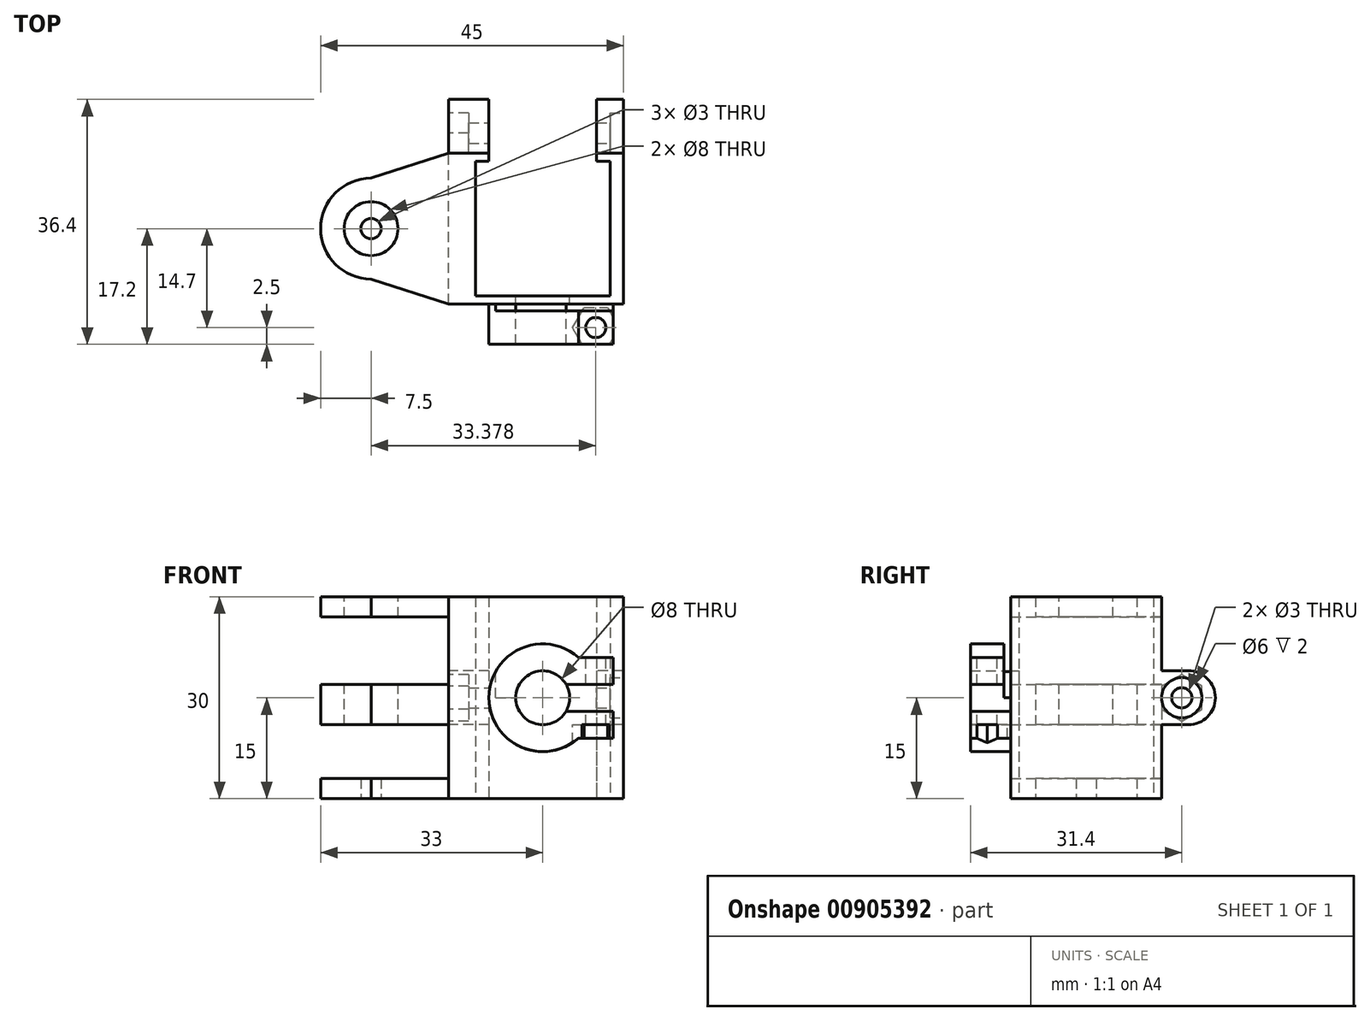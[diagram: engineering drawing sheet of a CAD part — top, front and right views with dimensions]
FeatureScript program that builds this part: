
annotation { "Feature Type Name" : "Feature", "Feature Type Description" : "" }
export const myFeature = defineFeature(function(context is Context, id is Id, definition is map)
    precondition{}
    {
        {
            var Q0;
            Q0=qCreatedBy(makeId("Top.planeOp"),FACE);
            var sketch = newSketch(context, id + "F0", { "sketchPlane" : qUnion([Q0])});
            skLineSegment(sketch, "E0.bottom", {"start": v(0, 0) * mm, "end": v(20, 0) * mm});
            skLineSegment(sketch, "E0.top", {"start": v(0, 20) * mm, "end": v(20, 20) * mm});
            skLineSegment(sketch, "E0.left", {"start": v(0, 0) * mm, "end": v(0, 20) * mm});
            skLineSegment(sketch, "E0.right", {"start": v(20, 0) * mm, "end": v(20, 20) * mm});
            skLineSegment(sketch, "E1.bottom", {"start": v(0, 0) * mm, "end": v(-4, 0) * mm, "construction": true});
            skLineSegment(sketch, "E1.top", {"start": v(0, -1.2) * mm, "end": v(-4, -1.2) * mm, "construction": true});
            skLineSegment(sketch, "E1.left", {"start": v(0, 0) * mm, "end": v(0, -1.2) * mm, "construction": true});
            skLineSegment(sketch, "E1.right", {"start": v(-4, 0) * mm, "end": v(-4, -1.2) * mm, "construction": true});
            skLineSegment(sketch, "E2.bottom", {"start": v(-4, -1.2) * mm, "end": v(22, -1.2) * mm});
            skLineSegment(sketch, "E2.top", {"start": v(-4, 21.2) * mm, "end": v(22, 21.2) * mm});
            skLineSegment(sketch, "E2.left", {"start": v(-4, -1.2) * mm, "end": v(-4, 21.2) * mm});
            skLineSegment(sketch, "E2.right", {"start": v(22, -1.2) * mm, "end": v(22, 21.2) * mm});
            skLineSegment(sketch, "E3", {"start": v(0, 20) * mm, "end": v(2, 20) * mm, "construction": true});
            skLineSegment(sketch, "E4", {"start": v(2, 20) * mm, "end": v(2, 21.2) * mm});
            skLineSegment(sketch, "E5", {"start": v(20, 20) * mm, "end": v(18, 20) * mm, "construction": true});
            skLineSegment(sketch, "E6", {"start": v(18, 20) * mm, "end": v(18, 21.2) * mm});
            skLineSegment(sketch, "E7.bottom", {"start": v(9, -1.2) * mm, "end": v(-6, -1.2) * mm, "construction": true});
            skLineSegment(sketch, "E7.top", {"start": v(9, 10) * mm, "end": v(-6, 10) * mm, "construction": true});
            skLineSegment(sketch, "E7.left", {"start": v(9, -1.2) * mm, "end": v(9, 10) * mm, "construction": true});
            skLineSegment(sketch, "E7.right", {"start": v(-6, -1.2) * mm, "end": v(-6, 10) * mm, "construction": true});
            skLineSegment(sketch, "E8", {"start": v(-6, 10) * mm, "end": v(-15.5, 10) * mm, "construction": true});
            skCircle(sketch, "E9", {"center": v(-15.5, 10) * mm, "radius": 7.5 * mm});
            skCircle(sketch, "E10", {"center": v(-15.5, 10) * mm, "radius": 1.5 * mm});
            skLineSegment(sketch, "E11", {"start": v(-15.5, 10) * mm, "end": v(-15.5, 17.5) * mm, "construction": true});
            skLineSegment(sketch, "E12", {"start": v(-15.5, 17.5) * mm, "end": v(-15.5, 2.5) * mm, "construction": true});
            skLineSegment(sketch, "E13", {"start": v(-4, -1.2) * mm, "end": v(-15.5, 2.5) * mm});
            skLineSegment(sketch, "E14", {"start": v(-4, 21.2) * mm, "end": v(-15.5, 17.5) * mm});
            skSolve(sketch);
        }
        {
            var Q0;
            Q0=makeQuery(id+"F0.imprint","IMPRINT",FACE,{"disambiguationData":[TD([[makeQuery(id+"F0.imprint","IMPRINT",EDGE,{"derivedFrom":sQuery(id+"F0.wireOp",EDGE,"E0.bottom")}),-1.0]])]});
            extrude(context, id + "F1", {"entities" : qUnion([Q0]), "depth" : 30 * mm, "offsetDistance" : 25 * mm});
        }
        {
            var Q0;
            Q0=makeQuery(id+"F1.opExtrude","SWEPT_FACE",FACE,{"disambiguationData":[OSD([sQuery(id+"F0.wireOp",EDGE,"E2.bottom")])]});
            var sketch = newSketch(context, id + "F2", { "sketchPlane" : qUnion([Q0])});
            skCircle(sketch, "E15", {"center": v(10, 15) * mm, "radius": 4 * mm});
            skCircle(sketch, "E16", {"center": v(10, 15) * mm, "radius": 8 * mm});
            skLineSegment(sketch, "E17", {"start": v(10, 15) * mm, "end": v(10, 13) * mm, "construction": true});
            skLineSegment(sketch, "E18", {"start": v(10, 13) * mm, "end": v(13.46, 13) * mm, "construction": true});
            skLineSegment(sketch, "E19", {"start": v(10, 15) * mm, "end": v(10, 17) * mm, "construction": true});
            skLineSegment(sketch, "E20", {"start": v(10, 17) * mm, "end": v(13.46, 17) * mm, "construction": true});
            skLineSegment(sketch, "E21", {"start": v(13.46, 17) * mm, "end": v(20.46, 17) * mm});
            skLineSegment(sketch, "E22", {"start": v(13.46, 17) * mm, "end": v(13.46, 21) * mm, "construction": true});
            skLineSegment(sketch, "E23", {"start": v(13.46, 21) * mm, "end": v(20.46, 21) * mm});
            skLineSegment(sketch, "E24", {"start": v(13.46, 13) * mm, "end": v(20.46, 13) * mm});
            skLineSegment(sketch, "E25", {"start": v(13.46, 13) * mm, "end": v(13.46, 9) * mm, "construction": true});
            skLineSegment(sketch, "E26", {"start": v(13.46, 9) * mm, "end": v(20.46, 9) * mm});
            skLineSegment(sketch, "E27", {"start": v(20.46, 9) * mm, "end": v(20.46, 13) * mm});
            skLineSegment(sketch, "E28", {"start": v(20.46, 21) * mm, "end": v(20.46, 17) * mm});
            skLineSegment(sketch, "E29", {"start": v(10, 15) * mm, "end": v(-4, 15) * mm});
            skSolve(sketch);
        }
        {
            var Q0;
            {var subQ5=sQuery(id+"F2.wireOp",EDGE,"E21");var subQ7=sQuery(id+"F2.wireOp",EDGE,"E15");var subQ8=makeQuery(id+"F2.imprint","INTERSECT",VERTEX,{"derivedFrom":[subQ7,subQ5]});Q0=makeQuery(id+"F2.imprint","IMPRINT",FACE,{"disambiguationData":[TD([[makeQuery(id+"F2.imprint","IMPRINT",EDGE,{"disambiguationData":[TD([[subQ8,-1.0]])],"derivedFrom":subQ7}),-1.0]])]});}
            var Q1;
            {var subQ5=sQuery(id+"F2.wireOp",EDGE,"E28");Q1=makeQuery(id+"F2.imprint","IMPRINT",FACE,{"disambiguationData":[TD([[makeQuery(id+"F2.imprint","IMPRINT",EDGE,{"derivedFrom":subQ5}),-1.0]])]});}
            var Q2;
            {var subQ5=sQuery(id+"F2.wireOp",EDGE,"E27");Q2=makeQuery(id+"F2.imprint","IMPRINT",FACE,{"disambiguationData":[TD([[makeQuery(id+"F2.imprint","IMPRINT",EDGE,{"derivedFrom":subQ5}),1.0]])]});}
            var Q3;
            {var subQ4=sQuery(id+"F2.wireOp",EDGE,"E15");var subQ6=sQuery(id+"F2.wireOp",EDGE,"E24");var subQ7=makeQuery(id+"F2.imprint","INTERSECT",VERTEX,{"derivedFrom":[subQ4,subQ6]});Q3=makeQuery(id+"F2.imprint","IMPRINT",FACE,{"disambiguationData":[TD([[makeQuery(id+"F2.imprint","IMPRINT",EDGE,{"disambiguationData":[TD([[subQ7,1.0]])],"derivedFrom":subQ4}),-1.0]])]});}
            extrude(context, id + "F3", {"entities" : qUnion([Q0, Q1, Q2, Q3]), "operationType" : NewBodyOperationType.ADD, "depth" : 6 * mm, "offsetDistance" : 25 * mm});
        }
        {
            var Q0;
            {var subQ0=sQuery(id+"F2.wireOp",EDGE,"E15");var subQ1=makeQuery(id+"F2.imprint","INTERSECT",VERTEX,{"derivedFrom":[subQ0,sQuery(id+"F2.wireOp",EDGE,"E21")]});Q0=makeQuery(id+"F2.imprint","IMPRINT",FACE,{"disambiguationData":[TD([[makeQuery(id+"F2.imprint","IMPRINT",EDGE,{"disambiguationData":[TD([[subQ1,-1.0]])],"derivedFrom":subQ0}),1.0]])]});}
            extrude(context, id + "F4", {"entities" : qUnion([Q0]), "operationType" : NewBodyOperationType.REMOVE, "oppositeDirection" : true, "depth" : 25 * mm, "offsetDistance" : 25 * mm});
        }
        {
            var Q0;
            Q0=makeQuery(id+"F1.opExtrude","CAP_FACE",FACE,{"disambiguationData":[OSD([sQuery(id+"F0.wireOp",EDGE,"E0.bottom"),sQuery(id+"F0.wireOp",EDGE,"E0.left"),sQuery(id+"F0.wireOp",EDGE,"E0.right"),sQuery(id+"F0.wireOp",EDGE,"E2.bottom"),sQuery(id+"F0.wireOp",EDGE,"E2.top"),sQuery(id+"F0.wireOp",EDGE,"E2.left"),sQuery(id+"F0.wireOp",EDGE,"E2.right"),sQuery(id+"F0.wireOp",EDGE,"0gwIZlqe-FvKl-Nv9Y-vsOx-YCTr08s2W5oZ"),sQuery(id+"F0.wireOp",EDGE,"uGnjY2x7-gKUO-HtRP-5AOL-VpCL24SmFymk")])],"isStart":false});
            var sketch = newSketch(context, id + "F5", { "sketchPlane" : qUnion([Q0])});
            skLineSegment(sketch, "E30", {"start": v(0, 0) * mm, "end": v(3, 0) * mm, "construction": true});
            skLineSegment(sketch, "E31", {"start": v(3, 0) * mm, "end": v(3, -1.2) * mm, "construction": true});
            skLineSegment(sketch, "E32.bottom", {"start": v(3, -1.2) * mm, "end": v(23, -1.2) * mm});
            skLineSegment(sketch, "E32.top", {"start": v(3, -2.2) * mm, "end": v(23, -2.2) * mm});
            skLineSegment(sketch, "E32.left", {"start": v(3, -1.2) * mm, "end": v(3, -2.2) * mm});
            skLineSegment(sketch, "E32.right", {"start": v(23, -1.2) * mm, "end": v(23, -2.2) * mm});
            skSolve(sketch);
        }
        {
            var Q0;
            Q0=makeQuery(id+"F5.imprint","IMPRINT",FACE,{"disambiguationData":[TD([[makeQuery(id+"F5.imprint","IMPRINT",EDGE,{"derivedFrom":sQuery(id+"F5.wireOp",EDGE,"E32.top")}),1.0]])]});
            extrude(context, id + "F6", {"entities" : qUnion([Q0]), "operationType" : NewBodyOperationType.REMOVE, "oppositeDirection" : true, "depth" : 15 * mm, "offsetDistance" : 25 * mm});
        }
        {
            var Q0;
            Q0=makeQuery(id+"F3.opExtrude","SWEPT_FACE",FACE,{"disambiguationData":[OSD([sQuery(id+"F2.wireOp",EDGE,"E23")])]});
            var sketch = newSketch(context, id + "F7", { "sketchPlane" : qUnion([Q0])});
            skLineSegment(sketch, "E33", {"start": v(17.88, -7.2) * mm, "end": v(17.88, -4.7) * mm, "construction": true});
            skCircle(sketch, "E34", {"center": v(17.88, -4.7) * mm, "radius": 1.5 * mm});
            skSolve(sketch);
        }
        {
            var Q0;
            Q0=makeQuery(id+"F7.imprint","IMPRINT",FACE,{"disambiguationData":[TD([[makeQuery(id+"F7.imprint","IMPRINT",EDGE,{"derivedFrom":sQuery(id+"F7.wireOp",EDGE,"E34")}),1.0]])]});
            extrude(context, id + "F8", {"entities" : qUnion([Q0]), "operationType" : NewBodyOperationType.REMOVE, "oppositeDirection" : true, "depth" : 25 * mm, "offsetDistance" : 25 * mm});
        }
        {
            var Q0;
            {var subQ0=sQuery(id+"F0.wireOp",EDGE,"E2.top");Q0=makeQuery(id+"F1.opExtrude","SWEPT_FACE",FACE,{"disambiguationData":[OSD([subQ0]),TDD([makeQuery(id+"F0.imprint","IMPRINT",EDGE,{"disambiguationData":[TD([[makeQuery(id+"F0.imprint","INTERSECT",VERTEX,{"derivedFrom":[subQ0,sQuery(id+"F0.wireOp",EDGE,"E2.right")]}),1.0]])],"derivedFrom":subQ0})])]});}
            var sketch = newSketch(context, id + "F9", { "sketchPlane" : qUnion([Q0])});
            skLineSegment(sketch, "E35", {"start": v(-22, 30) * mm, "end": v(-22, 19) * mm, "construction": true});
            skLineSegment(sketch, "E36.bottom", {"start": v(-22, 19) * mm, "end": v(-18, 19) * mm});
            skLineSegment(sketch, "E36.top", {"start": v(-22, 11) * mm, "end": v(-18, 11) * mm});
            skLineSegment(sketch, "E36.left", {"start": v(-22, 19) * mm, "end": v(-22, 11) * mm});
            skLineSegment(sketch, "E36.right", {"start": v(-18, 19) * mm, "end": v(-18, 11) * mm});
            skLineSegment(sketch, "E37", {"start": v(-18, 11) * mm, "end": v(-2, 11) * mm, "construction": true});
            skLineSegment(sketch, "E38.bottom", {"start": v(-2, 11) * mm, "end": v(4, 11) * mm});
            skLineSegment(sketch, "E38.top", {"start": v(-2, 19) * mm, "end": v(4, 19) * mm});
            skLineSegment(sketch, "E38.left", {"start": v(-2, 11) * mm, "end": v(-2, 19) * mm});
            skLineSegment(sketch, "E38.right", {"start": v(4, 11) * mm, "end": v(4, 19) * mm});
            skSolve(sketch);
        }
        {
            var Q0;
            Q0=makeQuery(id+"F9.imprint","IMPRINT",FACE,{"disambiguationData":[TD([[makeQuery(id+"F9.imprint","IMPRINT",EDGE,{"derivedFrom":sQuery(id+"F9.wireOp",EDGE,"E36.bottom")}),-1.0]])]});
            var Q1;
            Q1=makeQuery(id+"F9.imprint","IMPRINT",FACE,{"disambiguationData":[TD([[makeQuery(id+"F9.imprint","IMPRINT",EDGE,{"derivedFrom":sQuery(id+"F9.wireOp",EDGE,"E38.bottom")}),1.0]])]});
            extrude(context, id + "F10", {"entities" : qUnion([Q0, Q1]), "operationType" : NewBodyOperationType.ADD, "depth" : 8 * mm, "offsetDistance" : 25 * mm});
        }
        {
            var Q0;
            Q0=makeQuery(id+"F10.opExtrude","CAP_EDGE",EDGE,{"disambiguationData":[OSD([sQuery(id+"F9.wireOp",EDGE,"E36.bottom")])],"isStart":false});
            var Q1;
            Q1=makeQuery(id+"F10.opExtrude","CAP_EDGE",EDGE,{"disambiguationData":[OSD([sQuery(id+"F9.wireOp",EDGE,"E36.top")])],"isStart":false});
            var Q2;
            Q2=makeQuery(id+"F10.opExtrude","CAP_EDGE",EDGE,{"disambiguationData":[OSD([sQuery(id+"F9.wireOp",EDGE,"E38.top")])],"isStart":false});
            var Q3;
            Q3=makeQuery(id+"F10.opExtrude","CAP_EDGE",EDGE,{"disambiguationData":[OSD([sQuery(id+"F9.wireOp",EDGE,"E38.bottom")])],"isStart":false});
            fillet(context, id + "F11", {"entities" : qUnion([Q0, Q1, Q2, Q3]), "radius" : 4 * mm, "tangentPropagation" : true, "allowEdgeOverflow" : false});
        }
        {
            var Q0;
            Q0=makeQuery(id+"F10.boolean.opBoolean","MERGE",FACE,{"derivedFrom":[makeQuery(id+"F1.opExtrude","SWEPT_FACE",FACE,{"disambiguationData":[OSD([sQuery(id+"F0.wireOp",EDGE,"E2.right")])]}),makeQuery(id+"F10.opExtrude","SWEPT_FACE",FACE,{"disambiguationData":[OSD([sQuery(id+"F9.wireOp",EDGE,"E36.left")])]})]});
            var sketch = newSketch(context, id + "F12", { "sketchPlane" : qUnion([Q0])});
            skLineSegment(sketch, "E39.bottom", {"start": v(21.2, 19) * mm, "end": v(24.2, 19) * mm, "construction": true});
            skLineSegment(sketch, "E39.top", {"start": v(21.2, 15) * mm, "end": v(24.2, 15) * mm, "construction": true});
            skLineSegment(sketch, "E39.left", {"start": v(21.2, 19) * mm, "end": v(21.2, 15) * mm, "construction": true});
            skLineSegment(sketch, "E39.right", {"start": v(24.2, 19) * mm, "end": v(24.2, 15) * mm, "construction": true});
            skCircle(sketch, "E40", {"center": v(24.2, 15) * mm, "radius": 1.5 * mm});
            skCircle(sketch, "E41", {"center": v(24.2, 15) * mm, "radius": 3 * mm});
            skSolve(sketch);
        }
        {
            var Q0;
            Q0=makeQuery(id+"F12.imprint","IMPRINT",FACE,{"disambiguationData":[TD([[makeQuery(id+"F12.imprint","IMPRINT",EDGE,{"derivedFrom":sQuery(id+"F12.wireOp",EDGE,"U8nkkglx-LdFy-GuxK-7bps-SsXD2pFavUmK")}),1.0]])]});
            var Q1;
            Q1=makeQuery(id+"F12.imprint","IMPRINT",FACE,{"disambiguationData":[TD([[makeQuery(id+"F12.imprint","IMPRINT",EDGE,{"derivedFrom":sQuery(id+"F12.wireOp",EDGE,"E40")}),1.0]])]});
            extrude(context, id + "F13", {"entities" : qUnion([Q0, Q1]), "operationType" : NewBodyOperationType.REMOVE, "oppositeDirection" : true, "depth" : 25 * mm, "offsetDistance" : 25 * mm});
        }
        {
            var Q0;
            Q0=makeQuery(id+"F0.imprint","IMPRINT",FACE,{"disambiguationData":[TD([[makeQuery(id+"F0.imprint","IMPRINT",EDGE,{"derivedFrom":sQuery(id+"F0.wireOp",EDGE,"E2.left")}),1.0]])]});
            var Q1;
            Q1=makeQuery(id+"F0.imprint","IMPRINT",FACE,{"disambiguationData":[TD([[makeQuery(id+"F0.imprint","IMPRINT",EDGE,{"derivedFrom":sQuery(id+"F0.wireOp",EDGE,"E10")}),-1.0]])]});
            var Q2;
            Q2=makeQuery(id+"F0.imprint","IMPRINT",FACE,{"disambiguationData":[TD([[makeQuery(id+"F0.imprint","IMPRINT",EDGE,{"derivedFrom":sQuery(id+"F0.wireOp",EDGE,"E0.bottom")}),-1.0]])]});
            extrude(context, id + "F14", {"entities" : qUnion([Q0, Q1, Q2]), "operationType" : NewBodyOperationType.ADD, "depth" : 30 * mm, "offsetDistance" : 25 * mm, "hasSecondDirection" : true, "secondDirectionOppositeDirection" : false, "secondDirectionDepth" : 27 * mm});
        }
        {
            var Q0;
            Q0=makeQuery(id+"F0.imprint","IMPRINT",FACE,{"disambiguationData":[TD([[makeQuery(id+"F0.imprint","IMPRINT",EDGE,{"derivedFrom":sQuery(id+"F0.wireOp",EDGE,"E10")}),-1.0]])]});
            var Q1;
            Q1=makeQuery(id+"F0.imprint","IMPRINT",FACE,{"disambiguationData":[TD([[makeQuery(id+"F0.imprint","IMPRINT",EDGE,{"derivedFrom":sQuery(id+"F0.wireOp",EDGE,"E2.left")}),1.0]])]});
            extrude(context, id + "F15", {"entities" : qUnion([Q0, Q1]), "operationType" : NewBodyOperationType.ADD, "depth" : 17 * mm, "offsetDistance" : 25 * mm, "hasSecondDirection" : true, "secondDirectionOppositeDirection" : false, "secondDirectionDepth" : 11 * mm});
        }
        {
            var Q0;
            Q0=makeQuery(id+"F0.imprint","IMPRINT",FACE,{"disambiguationData":[TD([[makeQuery(id+"F0.imprint","IMPRINT",EDGE,{"derivedFrom":sQuery(id+"F0.wireOp",EDGE,"E10")}),-1.0]])]});
            var Q1;
            Q1=makeQuery(id+"F0.imprint","IMPRINT",FACE,{"disambiguationData":[TD([[makeQuery(id+"F0.imprint","IMPRINT",EDGE,{"derivedFrom":sQuery(id+"F0.wireOp",EDGE,"E2.left")}),1.0]])]});
            extrude(context, id + "F16", {"entities" : qUnion([Q0, Q1]), "operationType" : NewBodyOperationType.ADD, "depth" : 3 * mm, "offsetDistance" : 25 * mm});
        }
        {
            var Q0;
            {var subQ0=sQuery(id+"F0.wireOp",EDGE,"E6");var subQ1=sQuery(id+"F0.wireOp",EDGE,"E4");var subQ2=sQuery(id+"F0.wireOp",EDGE,"E2.right");var subQ3=sQuery(id+"F0.wireOp",EDGE,"E2.top");var subQ4=sQuery(id+"F0.wireOp",EDGE,"E2.bottom");var subQ5=sQuery(id+"F0.wireOp",EDGE,"E0.right");var subQ6=sQuery(id+"F0.wireOp",EDGE,"E0.left");var subQ7=sQuery(id+"F0.wireOp",EDGE,"E0.top");var subQ8=sQuery(id+"F0.wireOp",EDGE,"E0.bottom");Q0=makeQuery(id+"F14.boolean.opBoolean","MERGE",FACE,{"derivedFrom":[makeQuery(id+"F1.opExtrude","CAP_FACE",FACE,{"disambiguationData":[OSD([subQ8,subQ7,subQ6,subQ5,subQ4,subQ3,sQuery(id+"F0.wireOp",EDGE,"E2.left"),subQ2,subQ1,subQ0])],"isStart":false}),makeQuery(id+"F14.opExtrude","CAP_FACE",FACE,{"disambiguationData":[OSD([subQ8,subQ7,subQ6,subQ5,subQ4,subQ3,subQ2,subQ1,subQ0,sQuery(id+"F0.wireOp",EDGE,"E9"),sQuery(id+"F0.wireOp",EDGE,"E10"),sQuery(id+"F0.wireOp",EDGE,"E13"),sQuery(id+"F0.wireOp",EDGE,"E14")])],"isStart":false})]});}
            var sketch = newSketch(context, id + "F17", { "sketchPlane" : qUnion([Q0])});
            skCircle(sketch, "E42", {"center": v(-15.5, 10) * mm, "radius": 4 * mm});
            skSolve(sketch);
        }
        {
            var Q0;
            Q0=makeQuery(id+"F17.imprint","IMPRINT",FACE,{"disambiguationData":[TD([[makeQuery(id+"F17.imprint","IMPRINT",EDGE,{"derivedFrom":sQuery(id+"F17.wireOp",EDGE,"E42")}),1.0]])]});
            extrude(context, id + "F18", {"entities" : qUnion([Q0]), "operationType" : NewBodyOperationType.REMOVE, "oppositeDirection" : true, "depth" : 27 * mm, "offsetDistance" : 25 * mm});
        }
        {
            var Q0;
            Q0=makeQuery(id+"F12.imprint","IMPRINT",FACE,{"disambiguationData":[TD([[makeQuery(id+"F12.imprint","IMPRINT",EDGE,{"derivedFrom":sQuery(id+"F12.wireOp",EDGE,"E40")}),-1.0]])]});
            extrude(context, id + "F19", {"entities" : qUnion([Q0]), "operationType" : NewBodyOperationType.REMOVE, "oppositeDirection" : true, "depth" : 2 * mm, "offsetDistance" : 25 * mm});
        }
        {
            var Q0;
            {var subQ7=sQuery(id+"F0.wireOp",EDGE,"E2.left");var subQ8=makeQuery(id+"F1.opExtrude","SWEPT_FACE",FACE,{"disambiguationData":[OSD([subQ7])]});var subQ9=makeQuery(id+"F10.opExtrude","SWEPT_FACE",FACE,{"disambiguationData":[OSD([sQuery(id+"F9.wireOp",EDGE,"E38.right")])]});Q0=makeQuery(id+"F15.boolean.opBoolean","SPLIT",FACE,{"disambiguationData":[TD([makeQuery(id+"F10.opExtrude","SWEPT_FACE",FACE,{"disambiguationData":[OSD([sQuery(id+"F9.wireOp",EDGE,"E38.top")])]})])],"derivedFrom":makeQuery(id+"F10.boolean.opBoolean","MERGE",FACE,{"derivedFrom":[subQ8,subQ9]})});}
            var sketch = newSketch(context, id + "F20", { "sketchPlane" : qUnion([Q0])});
            skLineSegment(sketch, "E43", {"start": v(-21.2, 11) * mm, "end": v(-21.2, 15) * mm, "construction": true});
            skLineSegment(sketch, "E44", {"start": v(-21.2, 15) * mm, "end": v(-24.2, 15) * mm, "construction": true});
            skCircle(sketch, "E45.cCircle", {"center": v(-24.2, 15) * mm, "radius": 3 * mm, "construction": true});
            skLineSegment(sketch, "E45.0", {"start": v(-21.2, 16.73) * mm, "end": v(-21.2, 13.27) * mm});
            skLineSegment(sketch, "E45.1", {"start": v(-21.2, 13.27) * mm, "end": v(-24.2, 11.54) * mm});
            skLineSegment(sketch, "E45.2", {"start": v(-24.2, 11.54) * mm, "end": v(-27.2, 13.27) * mm});
            skLineSegment(sketch, "E45.3", {"start": v(-27.2, 13.27) * mm, "end": v(-27.2, 16.73) * mm});
            skLineSegment(sketch, "E45.4", {"start": v(-27.2, 16.73) * mm, "end": v(-24.2, 18.46) * mm});
            skLineSegment(sketch, "E45.5", {"start": v(-24.2, 18.46) * mm, "end": v(-21.2, 16.73) * mm});
            skPoint(sketch, "E45.0.midPoint", {"position": v(-21.2, 15) * mm});
            skSolve(sketch);
        }
        {
            var Q0;
            Q0=makeQuery(id+"F20.imprint","IMPRINT",FACE,{"disambiguationData":[TD([[makeQuery(id+"F20.imprint","IMPRINT",EDGE,{"derivedFrom":sQuery(id+"F20.wireOp",EDGE,"E45.0")}),-1.0]])]});
            extrude(context, id + "F21", {"entities" : qUnion([Q0]), "operationType" : NewBodyOperationType.REMOVE, "oppositeDirection" : true, "depth" : 3 * mm, "offsetDistance" : 25 * mm});
        }
        {
            var Q0;
            Q0=makeQuery(id+"F3.opExtrude","SWEPT_FACE",FACE,{"disambiguationData":[OSD([sQuery(id+"F2.wireOp",EDGE,"E24")])]});
            var sketch = newSketch(context, id + "F22", { "sketchPlane" : qUnion([Q0])});
            skLineSegment(sketch, "E46", {"start": v(17.88, -4.7) * mm, "end": v(17.88, -1.7) * mm, "construction": true});
            skCircle(sketch, "E47.cCircle", {"center": v(17.88, -4.7) * mm, "radius": 3 * mm, "construction": true});
            skLineSegment(sketch, "E47.0", {"start": v(16.15, -1.7) * mm, "end": v(19.6, -1.7) * mm});
            skLineSegment(sketch, "E47.1", {"start": v(19.6, -1.7) * mm, "end": v(21.34, -4.7) * mm});
            skLineSegment(sketch, "E47.2", {"start": v(21.34, -4.7) * mm, "end": v(19.6, -7.7) * mm});
            skLineSegment(sketch, "E47.3", {"start": v(19.6, -7.7) * mm, "end": v(16.15, -7.7) * mm});
            skLineSegment(sketch, "E47.4", {"start": v(16.15, -7.7) * mm, "end": v(14.41, -4.7) * mm});
            skLineSegment(sketch, "E47.5", {"start": v(14.41, -4.7) * mm, "end": v(16.15, -1.7) * mm});
            skPoint(sketch, "E47.0.midPoint", {"position": v(17.88, -1.7) * mm});
            skSolve(sketch);
        }
        {
            var Q0;
            {var subQ11=sQuery(id+"F22.wireOp",EDGE,"E47.0");Q0=makeQuery(id+"F22.imprint","IMPRINT",FACE,{"disambiguationData":[TD([[makeQuery(id+"F22.imprint","IMPRINT",EDGE,{"derivedFrom":subQ11}),-1.0]])]});}
            extrude(context, id + "F23", {"entities" : qUnion([Q0]), "operationType" : NewBodyOperationType.REMOVE, "oppositeDirection" : true, "depth" : 10 * mm, "offsetDistance" : 25 * mm, "hasSecondDirection" : true, "secondDirectionOppositeDirection" : true, "secondDirectionDepth" : 2 * mm});
        }
    });
